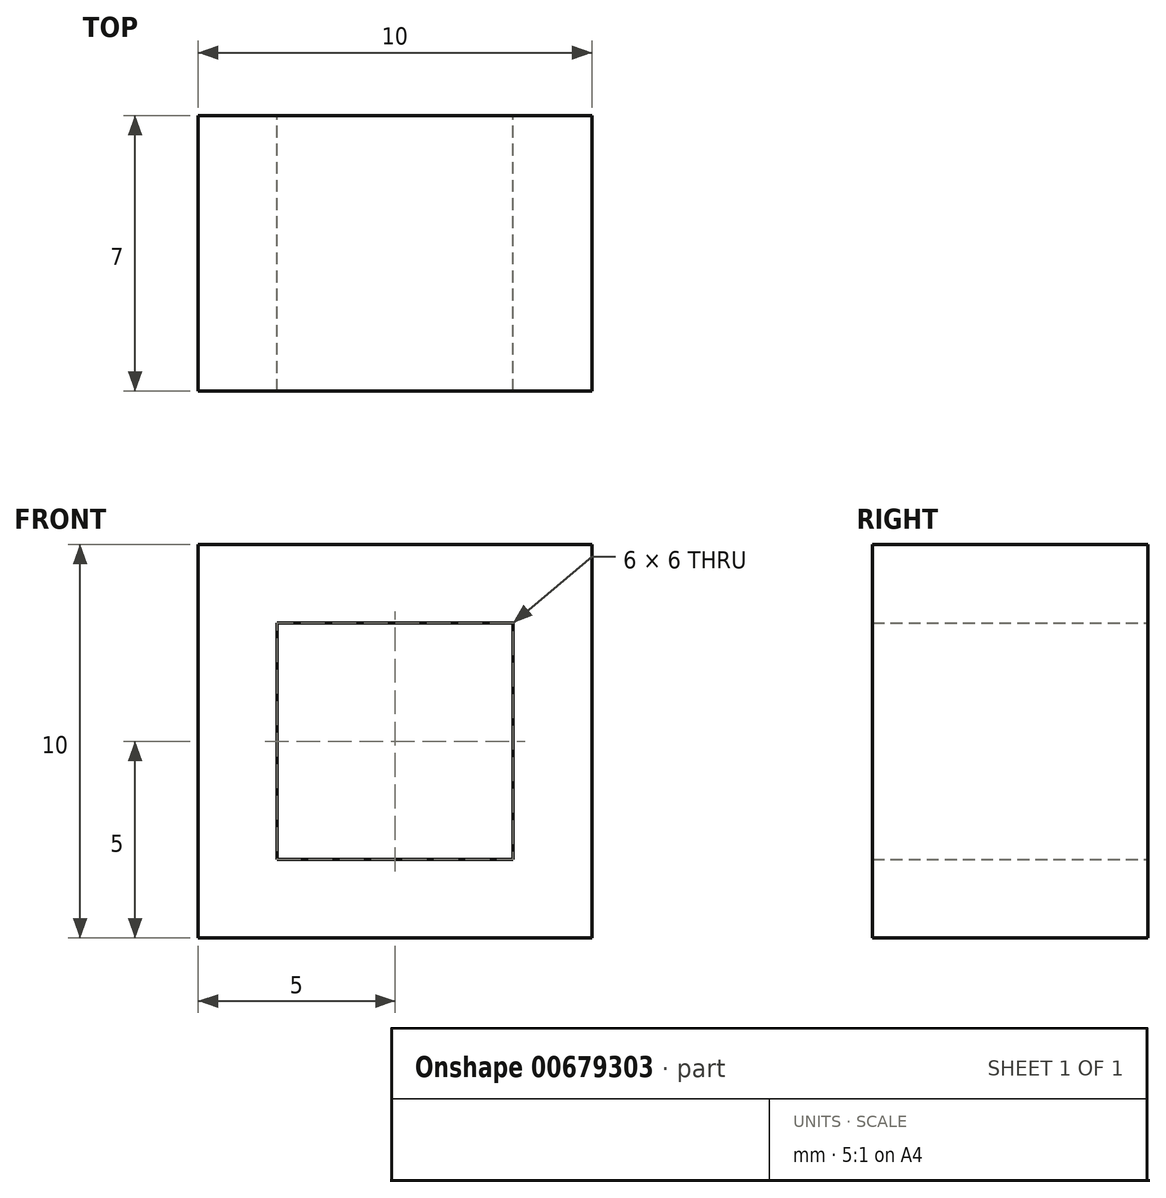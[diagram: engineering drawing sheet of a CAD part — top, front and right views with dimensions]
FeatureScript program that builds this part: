
annotation { "Feature Type Name" : "Feature", "Feature Type Description" : "" }
export const myFeature = defineFeature(function(context is Context, id is Id, definition is map)
    precondition{}
    {
        {
            var Q0;
            Q0=qCreatedBy(makeId("Front.planeOp"),FACE);
            var sketch = newSketch(context, id + "F0", { "sketchPlane" : qUnion([Q0])});
            skLineSegment(sketch, "E0.bottom", {"start": v(0, 0) * mm, "end": v(-10, 0) * mm});
            skLineSegment(sketch, "E0.top", {"start": v(0, 10) * mm, "end": v(-10, 10) * mm});
            skLineSegment(sketch, "E0.left", {"start": v(0, 0) * mm, "end": v(0, 10) * mm});
            skLineSegment(sketch, "E0.right", {"start": v(-10, 0) * mm, "end": v(-10, 10) * mm});
            skLineSegment(sketch, "E1.bottom", {"start": v(-8, 8) * mm, "end": v(-2, 8) * mm});
            skLineSegment(sketch, "E1.top", {"start": v(-8, 2) * mm, "end": v(-2, 2) * mm});
            skLineSegment(sketch, "E1.left", {"start": v(-8, 8) * mm, "end": v(-8, 2) * mm});
            skLineSegment(sketch, "E1.right", {"start": v(-2, 8) * mm, "end": v(-2, 2) * mm});
            skSolve(sketch);
        }
        {
            var Q0;
            Q0 = qSketchRegion(id + "F0", true);
            extrude(context, id + "F1", {"entities" : qUnion([Q0]), "depth" : 7 * mm, "offsetDistance" : 25 * mm});
        }
    });
